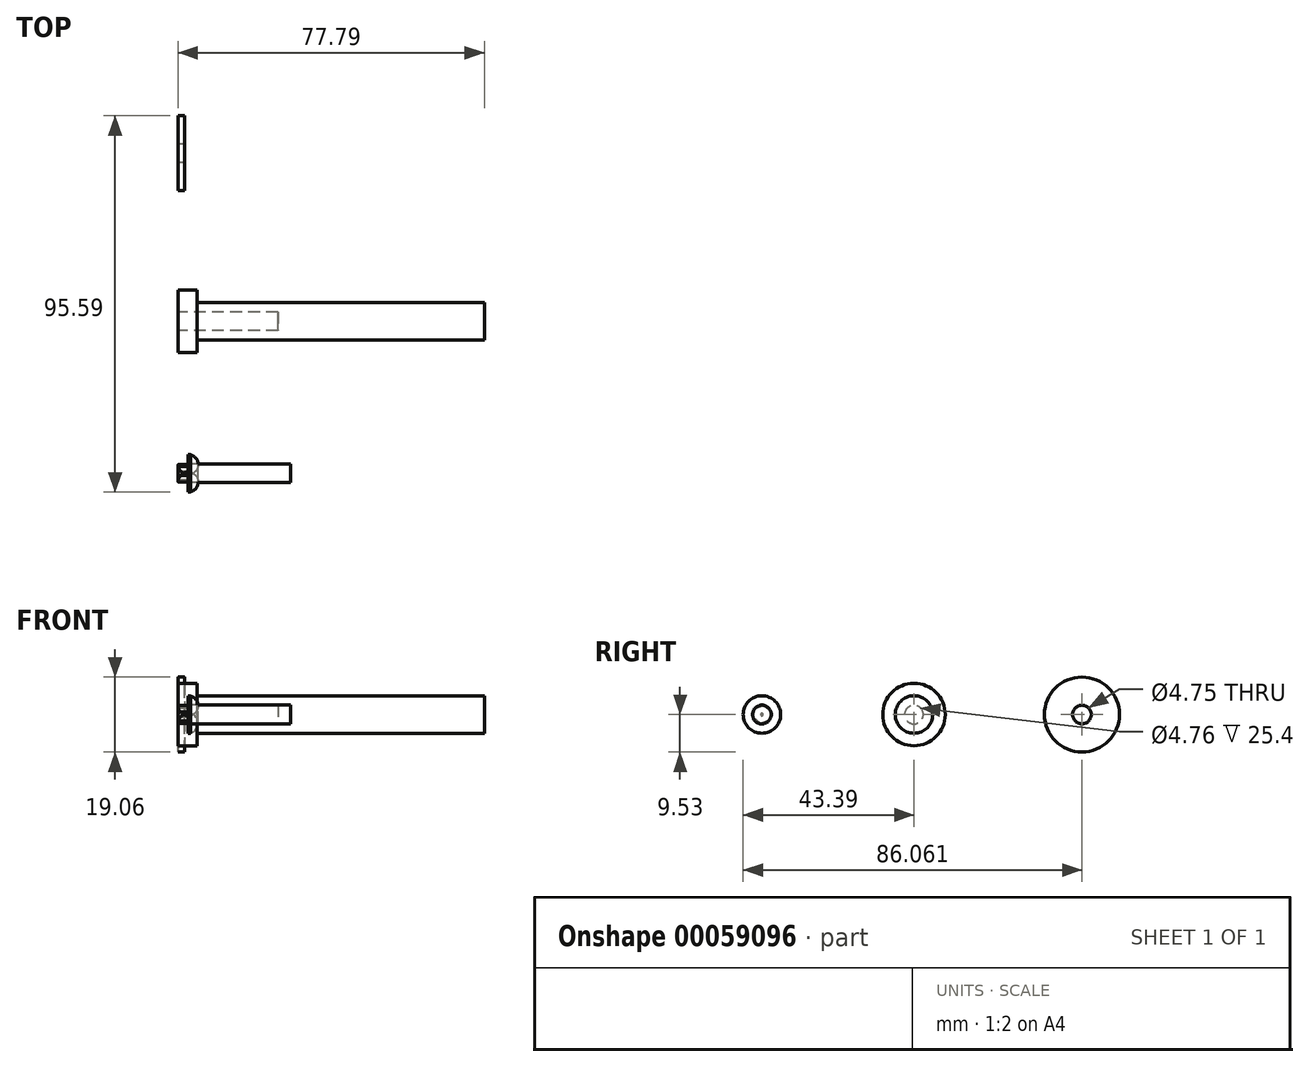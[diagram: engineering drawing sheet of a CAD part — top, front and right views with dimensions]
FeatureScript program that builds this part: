
annotation { "Feature Type Name" : "Feature", "Feature Type Description" : "" }
export const myFeature = defineFeature(function(context is Context, id is Id, definition is map)
    precondition{}
    {
        {
            var Q0;
            Q0=qCreatedBy(makeId("Right.planeOp"),FACE);
            var sketch = newSketch(context, id + "F0", { "sketchPlane" : qUnion([Q0])});
            skCircle(sketch, "E0", {"center": v(0, 0) * mm, "radius": 7.94 * mm});
            skSolve(sketch);
        }
        {
            var Q0;
            Q0=makeQuery(id+"F0.imprint","IMPRINT",FACE,{"disambiguationData":[TD([[makeQuery(id+"F0.imprint","IMPRINT",EDGE,{"derivedFrom":sQuery(id+"F0.wireOp",EDGE,"E0")}),1.0]])]});
            extrude(context, id + "F1", {"entities" : qUnion([Q0]), "depth" : 4.76 * mm});
        }
        {
            var Q0;
            Q0=makeQuery(id+"F1.opExtrude","CAP_FACE",FACE,{"disambiguationData":[OSD([sQuery(id+"F0.wireOp",EDGE,"E0")])],"isStart":false});
            var sketch = newSketch(context, id + "F2", { "sketchPlane" : qUnion([Q0])});
            skCircle(sketch, "E1", {"center": v(0, 0) * mm, "radius": 4.76 * mm});
            skSolve(sketch);
        }
        {
            var Q0;
            Q0=makeQuery(id+"F2.imprint","IMPRINT",FACE,{"disambiguationData":[TD([[makeQuery(id+"F2.imprint","IMPRINT",EDGE,{"derivedFrom":sQuery(id+"F2.wireOp",EDGE,"E1")}),1.0]])]});
            extrude(context, id + "F3", {"entities" : qUnion([Q0]), "operationType" : NewBodyOperationType.ADD, "depth" : 73.02 * mm});
        }
        {
            var Q0;
            Q0=makeQuery(id+"F1.opExtrude","CAP_FACE",FACE,{"disambiguationData":[OSD([sQuery(id+"F0.wireOp",EDGE,"E0")])],"isStart":true});
            var sketch = newSketch(context, id + "F4", { "sketchPlane" : qUnion([Q0])});
            skCircle(sketch, "E2", {"center": v(0, 0) * mm, "radius": 2.38 * mm});
            skSolve(sketch);
        }
        {
            var Q0;
            Q0=makeQuery(id+"F4.imprint","IMPRINT",FACE,{"disambiguationData":[TD([[makeQuery(id+"F4.imprint","IMPRINT",EDGE,{"derivedFrom":sQuery(id+"F4.wireOp",EDGE,"E2")}),1.0]])]});
            extrude(context, id + "F5", {"entities" : qUnion([Q0]), "operationType" : NewBodyOperationType.REMOVE, "oppositeDirection" : true, "depth" : 25.4 * mm});
        }
        {
            var Q0;
            Q0=qCreatedBy(makeId("Right.planeOp"),FACE);
            var sketch = newSketch(context, id + "F6", { "sketchPlane" : qUnion([Q0])});
            skCircle(sketch, "E3", {"center": v(42.67, 0) * mm, "radius": 9.53 * mm});
            skCircle(sketch, "E4", {"center": v(42.67, 0) * mm, "radius": 2.37 * mm});
            skSolve(sketch);
        }
        {
            var Q0;
            Q0=makeQuery(id+"F6.imprint","IMPRINT",FACE,{"disambiguationData":[TD([[makeQuery(id+"F6.imprint","IMPRINT",EDGE,{"derivedFrom":sQuery(id+"F6.wireOp",EDGE,"E3")}),1.0]])]});
            extrude(context, id + "F7", {"entities" : qUnion([Q0]), "depth" : 1.57 * mm});
        }
        {
            var Q0;
            Q0=qCreatedBy(makeId("Right.planeOp"),FACE);
            var sketch = newSketch(context, id + "F8", { "sketchPlane" : qUnion([Q0])});
            skCircle(sketch, "E5.cCircle", {"center": v(-38.63, 0) * mm, "radius": 3.17 * mm, "construction": true});
            skCircle(sketch, "E6", {"center": v(-38.63, 0) * mm, "radius": 4.76 * mm});
            skCircle(sketch, "E7.cCircle", {"center": v(-38.63, 0) * mm, "radius": 2.03 * mm, "construction": true});
            skLineSegment(sketch, "E7.0", {"start": v(-39.14, -2.3) * mm, "end": v(-40.87, -0.7) * mm});
            skLineSegment(sketch, "E7.1", {"start": v(-40.87, -0.7) * mm, "end": v(-40.36, 1.59) * mm});
            skLineSegment(sketch, "E7.2", {"start": v(-40.36, 1.59) * mm, "end": v(-38.12, 2.3) * mm});
            skLineSegment(sketch, "E7.3", {"start": v(-38.12, 2.3) * mm, "end": v(-36.39, 0.7) * mm});
            skLineSegment(sketch, "E7.4", {"start": v(-36.39, 0.7) * mm, "end": v(-36.9, -1.59) * mm});
            skLineSegment(sketch, "E7.5", {"start": v(-36.9, -1.59) * mm, "end": v(-39.14, -2.3) * mm});
            skPoint(sketch, "E7.0.midPoint", {"position": v(-40, -1.5) * mm});
            skSolve(sketch);
        }
        {
            var Q0;
            Q0=makeQuery(id+"F8.imprint","IMPRINT",FACE,{"disambiguationData":[TD([[makeQuery(id+"F8.imprint","IMPRINT",EDGE,{"derivedFrom":sQuery(id+"F8.wireOp",EDGE,"E6")}),1.0]])]});
            extrude(context, id + "F9", {"entities" : qUnion([Q0]), "depth" : 3.17 * mm});
        }
        {
            var Q0;
            Q0=makeQuery(id+"F9.opExtrude","CAP_FACE",FACE,{"disambiguationData":[OSD([sQuery(id+"F8.wireOp",EDGE,"E6"),sQuery(id+"F8.wireOp",EDGE,"E7.0"),sQuery(id+"F8.wireOp",EDGE,"E7.1"),sQuery(id+"F8.wireOp",EDGE,"E7.2"),sQuery(id+"F8.wireOp",EDGE,"E7.3"),sQuery(id+"F8.wireOp",EDGE,"E7.4"),sQuery(id+"F8.wireOp",EDGE,"E7.5")])],"isStart":false});
            var sketch = newSketch(context, id + "F10", { "sketchPlane" : qUnion([Q0])});
            skCircle(sketch, "E8", {"center": v(-38.63, 0) * mm, "radius": 2.38 * mm});
            skSolve(sketch);
        }
        {
            var Q0;
            Q0=makeQuery(id+"F10.imprint","IMPRINT",FACE,{"disambiguationData":[TD([[makeQuery(id+"F10.imprint","IMPRINT",EDGE,{"derivedFrom":sQuery(id+"F10.wireOp",EDGE,"E8")}),1.0]])]});
            var Q1;
            Q1=makeQuery(id+"F10.imprint","IMPRINT",FACE,{"disambiguationData":[TD([[makeQuery(id+"F10.imprint","IMPRINT",EDGE,{"derivedFrom":makeQuery(id+"F9.opExtrude","CAP_EDGE",EDGE,{"disambiguationData":[OSD([sQuery(id+"F8.wireOp",EDGE,"E7.0")])],"isStart":false})}),-1.0]])]});
            extrude(context, id + "F11", {"entities" : qUnion([Q0, Q1]), "operationType" : NewBodyOperationType.ADD, "depth" : 25.4 * mm});
        }
        {
            var Q0;
            Q0=makeQuery(id+"F9.opExtrude","CAP_EDGE",EDGE,{"disambiguationData":[OSD([sQuery(id+"F8.wireOp",EDGE,"E6")])],"isStart":true});
            fillet(context, id + "F12", {"entities" : qUnion([Q0]), "radius" : 2.54 * mm, "tangentPropagation" : true, "allowEdgeOverflow" : false});
        }
    });
